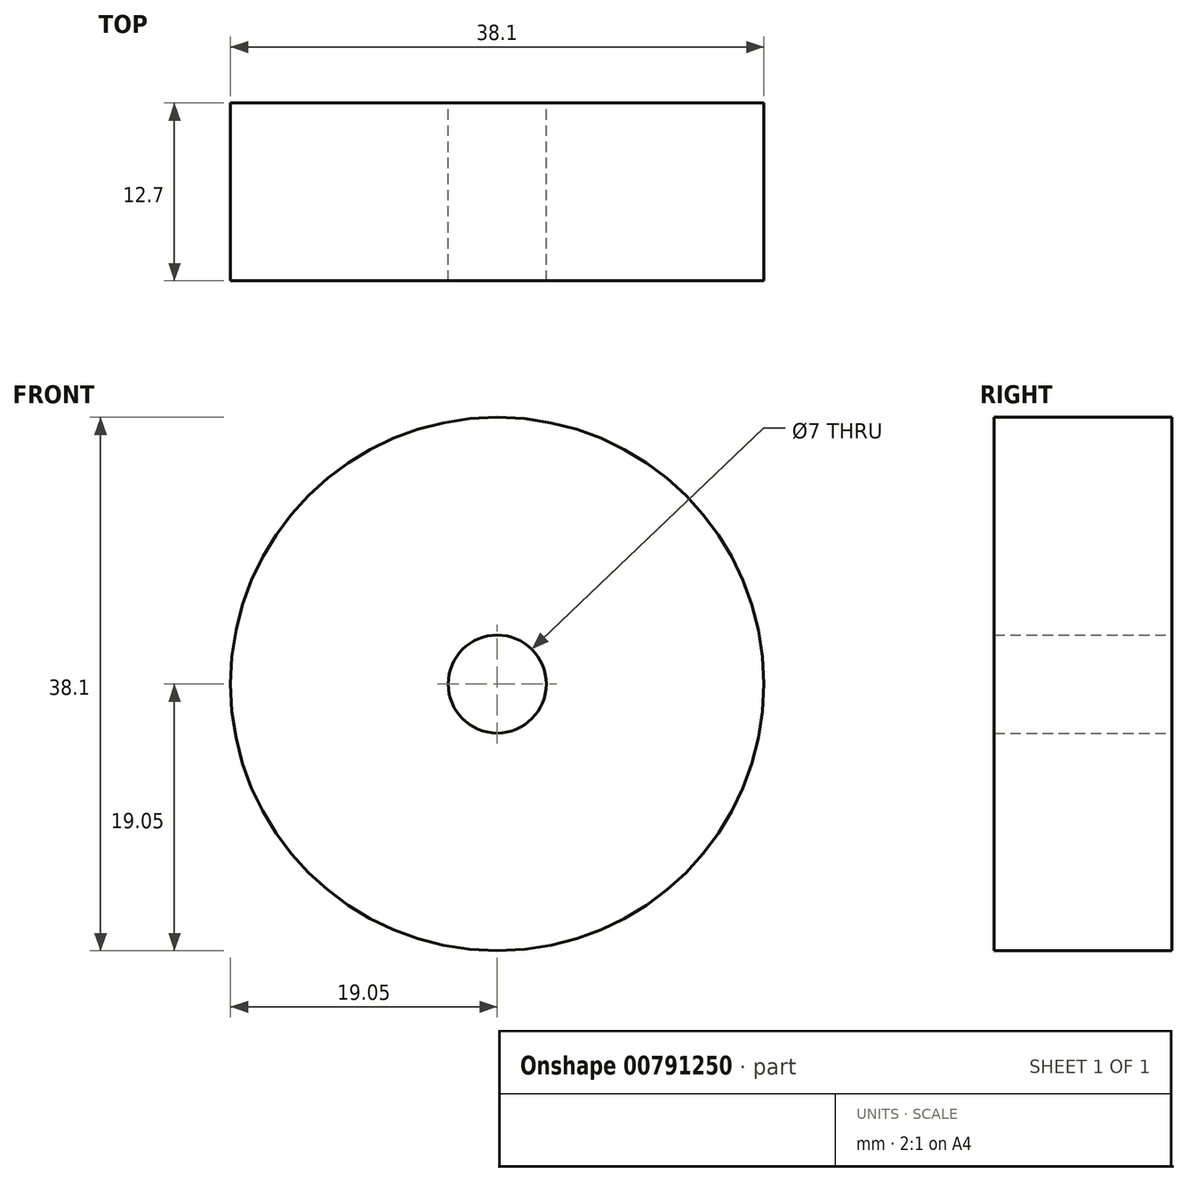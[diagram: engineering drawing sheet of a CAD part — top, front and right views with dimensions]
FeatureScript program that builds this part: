
annotation { "Feature Type Name" : "Feature", "Feature Type Description" : "" }
export const myFeature = defineFeature(function(context is Context, id is Id, definition is map)
    precondition{}
    {
        {
            var Q0;
            Q0=qCreatedBy(makeId("Front.planeOp"),FACE);
            var sketch = newSketch(context, id + "F0", { "sketchPlane" : qUnion([Q0])});
            skCircle(sketch, "E0", {"center": v(0, 0) * mm, "radius": 19.05 * mm});
            skCircle(sketch, "E1", {"center": v(0, 0) * mm, "radius": 3.5 * mm});
            skSolve(sketch);
        }
        {
            var Q0;
            Q0=qSketchRegion(id+"F0",true);
            extrude(context, id + "F1", {"entities" : qUnion([Q0]), "depth" : 12.7 * mm, "offsetDistance" : 25 * mm});
        }
    });
